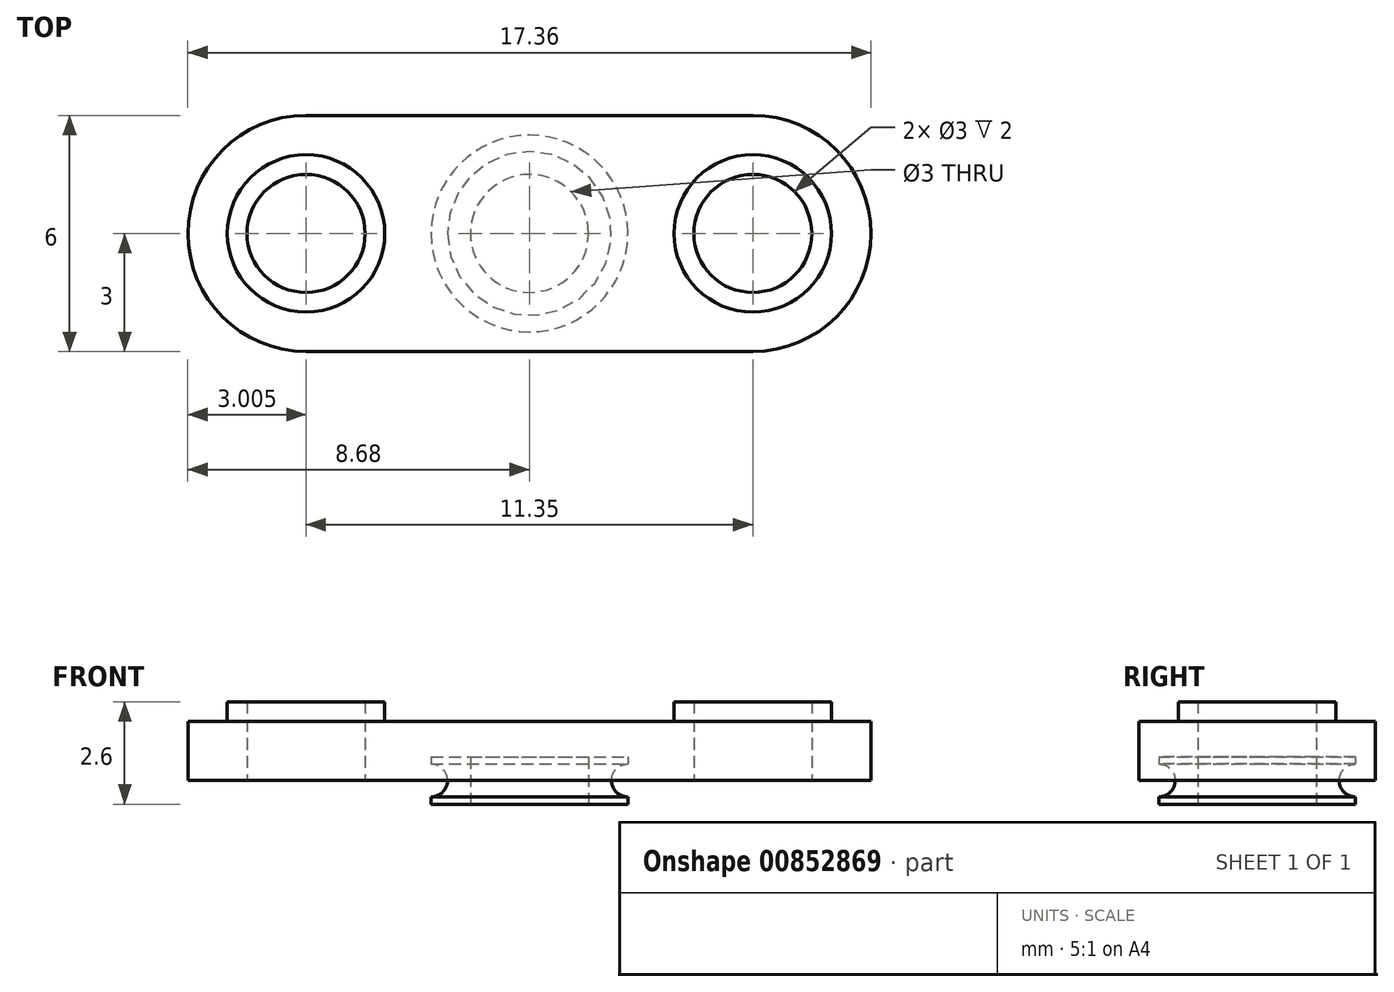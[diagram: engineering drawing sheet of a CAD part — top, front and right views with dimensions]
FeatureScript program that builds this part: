
annotation { "Feature Type Name" : "Feature", "Feature Type Description" : "" }
export const myFeature = defineFeature(function(context is Context, id is Id, definition is map)
    precondition{}
    {
        {
            var Q0;
            Q0=qCreatedBy(makeId("Top.planeOp"),FACE);
            var sketch = newSketch(context, id + "F0", { "sketchPlane" : qUnion([Q0])});
            skArc(sketch, "E0", {"start": v(-5.68, 3) * mm, "mid": v(-8.68, 0) * mm, "end": v(-5.67, -3) * mm});
            skLineSegment(sketch, "E1", {"start": v(-5.68, 3) * mm, "end": v(0, 3) * mm});
            skLineSegment(sketch, "E2", {"start": v(-5.68, -3) * mm, "end": v(0, -3) * mm});
            skLineSegment(sketch, "E3.MirrorCS", {"start": v(5.68, 3) * mm, "end": v(0, 3) * mm});
            skArc(sketch, "E4.MirrorCS", {"start": v(5.68, 3) * mm, "mid": v(8.68, 0) * mm, "end": v(5.67, -3) * mm});
            skLineSegment(sketch, "E5.MirrorCS", {"start": v(5.68, -3) * mm, "end": v(0, -3) * mm});
            skCircle(sketch, "E6", {"center": v(-5.68, 0) * mm, "radius": 1.5 * mm});
            skCircle(sketch, "E7.MirrorC", {"center": v(5.68, 0) * mm, "radius": 1.5 * mm});
            skSolve(sketch);
        }
        {
            var Q0;
            Q0=makeQuery(id+"F0.imprint","IMPRINT",FACE,{"disambiguationData":[TD([[makeQuery(id+"F0.imprint","IMPRINT",EDGE,{"derivedFrom":sQuery(id+"F0.wireOp",EDGE,"E0")}),1.0]])]});
            extrude(context, id + "F1", {"entities" : qUnion([Q0]), "depth" : 1.5 * mm, "offsetDistance" : 25 * mm});
        }
        {
            var Q0;
            Q0=makeQuery(id+"F1.opExtrude","CAP_FACE",FACE,{"disambiguationData":[OSD([sQuery(id+"F0.wireOp",EDGE,"E0"),sQuery(id+"F0.wireOp",EDGE,"E1"),sQuery(id+"F0.wireOp",EDGE,"E2"),sQuery(id+"F0.wireOp",EDGE,"E3.MirrorCS"),sQuery(id+"F0.wireOp",EDGE,"E4.MirrorCS"),sQuery(id+"F0.wireOp",EDGE,"E5.MirrorCS"),sQuery(id+"F0.wireOp",EDGE,"E6"),sQuery(id+"F0.wireOp",EDGE,"E7.MirrorC")])],"isStart":false});
            var sketch = newSketch(context, id + "F2", { "sketchPlane" : qUnion([Q0])});
            skCircle(sketch, "E8.0", {"center": v(-5.68, 0) * mm, "radius": 1.5 * mm});
            skCircle(sketch, "E9.0", {"center": v(5.68, 0) * mm, "radius": 1.5 * mm});
            skCircle(sketch, "E10", {"center": v(-5.68, 0) * mm, "radius": 2 * mm});
            skCircle(sketch, "E11.MirrorC", {"center": v(5.68, 0) * mm, "radius": 2 * mm});
            skSolve(sketch);
        }
        {
            var Q0;
            Q0 = qSketchRegion(id + "F2", true);
            extrude(context, id + "F3", {"entities" : qUnion([Q0]), "operationType" : NewBodyOperationType.ADD, "depth" : .5 * mm, "offsetDistance" : 25 * mm});
        }
        {
            var Q0;
            Q0=qCreatedBy(makeId("Front.planeOp"),FACE);
            var sketch = newSketch(context, id + "F4", { "sketchPlane" : qUnion([Q0])});
            skLineSegment(sketch, "E12", {"start": v(1.5, 0) * mm, "end": v(1.5, 0.6) * mm});
            skLineSegment(sketch, "E13", {"start": v(1.5, 0.6) * mm, "end": v(2.5, 0.6) * mm});
            skArc(sketch, "E14", {"start": v(2.5, 0.42) * mm, "mid": v(2.2, 0.3) * mm, "end": v(2.08, 0) * mm});
            skLineSegment(sketch, "E15", {"start": v(2.5, 0.6) * mm, "end": v(2.5, 0.42) * mm});
            skArc(sketch, "E16.MirrorCS", {"start": v(2.5, -0.42) * mm, "mid": v(2.2, -0.3) * mm, "end": v(2.08, 0) * mm});
            skLineSegment(sketch, "E17.MirrorCS", {"start": v(1.5, 0) * mm, "end": v(1.5, -0.6) * mm});
            skLineSegment(sketch, "E18.MirrorCS", {"start": v(2.5, -0.6) * mm, "end": v(2.5, -0.42) * mm});
            skLineSegment(sketch, "E19.MirrorCS", {"start": v(1.5, -0.6) * mm, "end": v(2.5, -0.6) * mm});
            skLineSegment(sketch, "E20", {"start": v(0, 0) * mm, "end": v(0, 0.64) * mm, "construction": true});
            skSolve(sketch);
        }
        {
            var Q0;
            Q0 = qSketchRegion(id + "F4", true);
            var Q1;
            Q1=sQuery(id+"F4.wireOp",EDGE,"E20");
            revolve(context, id + "F5", {"surfaceOperationType" : NewSurfaceOperationType.NEW, "entities" : qUnion([Q0]), "axis" : qUnion([Q1]), "revolveType" : RevolveType.FULL});
        }
    });
